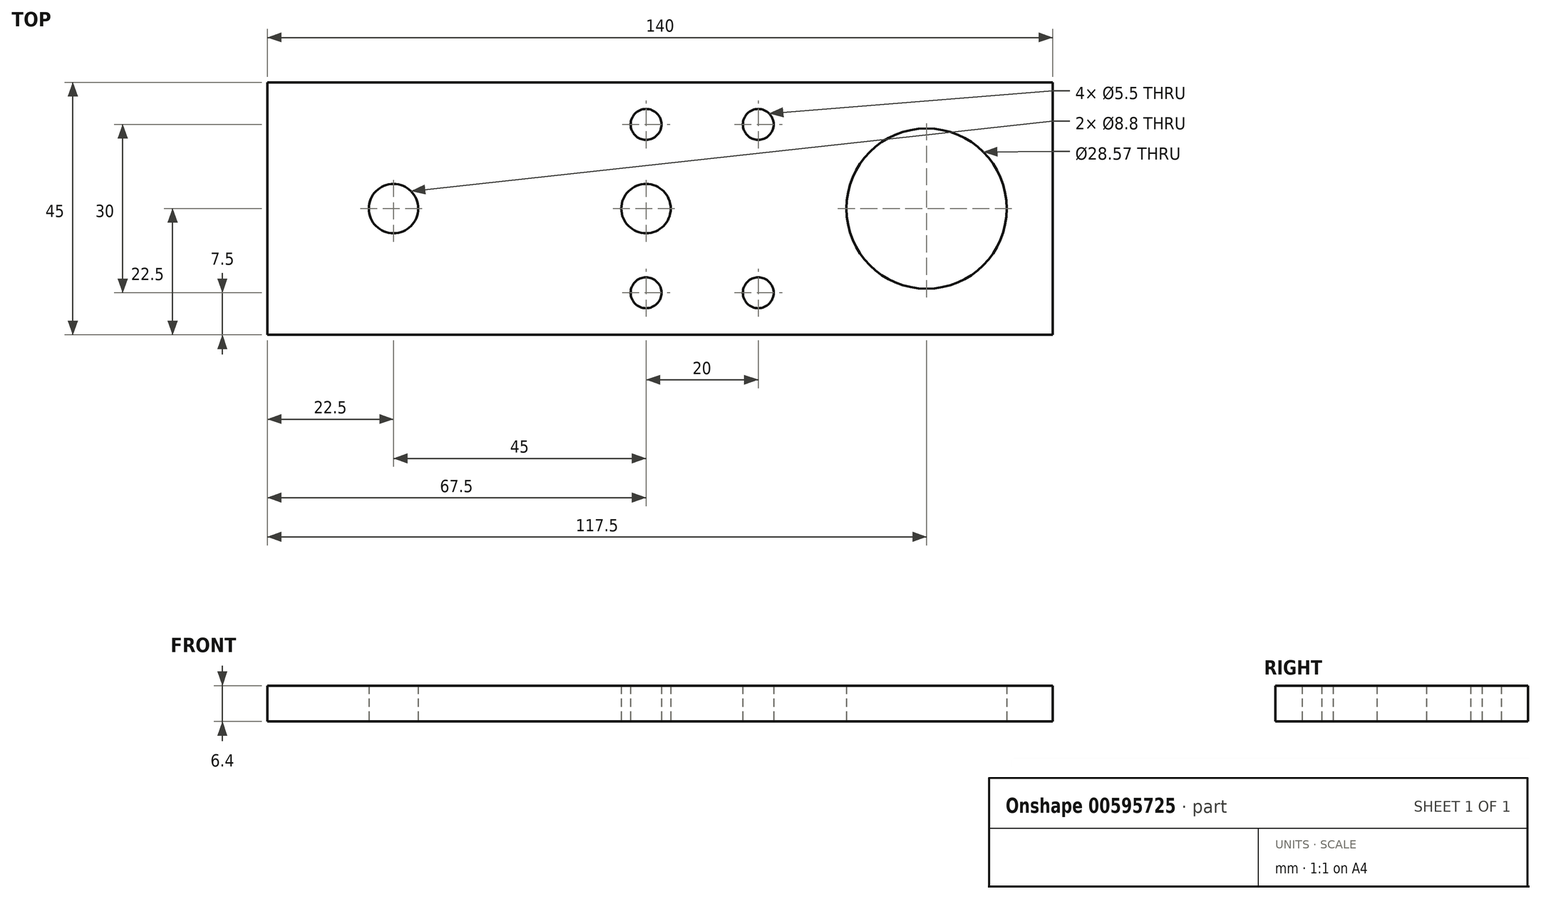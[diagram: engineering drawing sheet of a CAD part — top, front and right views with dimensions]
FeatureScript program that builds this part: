
annotation { "Feature Type Name" : "Feature", "Feature Type Description" : "" }
export const myFeature = defineFeature(function(context is Context, id is Id, definition is map)
    precondition{}
    {
        {
            var Q0;
            Q0=qCreatedBy(makeId("Top.planeOp"),FACE);
            var sketch = newSketch(context, id + "F0", { "sketchPlane" : qUnion([Q0])});
            skLineSegment(sketch, "E0.bottom", {"start": v(-70, 22.5) * mm, "end": v(70, 22.5) * mm});
            skLineSegment(sketch, "E0.top", {"start": v(-70, -22.5) * mm, "end": v(70, -22.5) * mm});
            skLineSegment(sketch, "E0.left", {"start": v(-70, 22.5) * mm, "end": v(-70, -22.5) * mm});
            skLineSegment(sketch, "E0.right", {"start": v(70, 22.5) * mm, "end": v(70, -22.5) * mm});
            skPoint(sketch, "E0.middle", {"position": v(0, 0) * mm});
            skCircle(sketch, "E1", {"center": v(47.5, 0) * mm, "radius": 14.29 * mm});
            skSolve(sketch);
        }
        {
            var Q0;
            Q0 = qSketchRegion(id + "F0", true);
            extrude(context, id + "F1", {"entities" : qUnion([Q0]), "depth" : 6.4 * mm, "offsetDistance" : 25 * mm});
        }
        {
            var Q0;
            Q0=makeQuery(id+"F1.opExtrude","CAP_FACE",FACE,{"disambiguationData":[OSD([sQuery(id+"F0.wireOp",EDGE,"E0.bottom"),sQuery(id+"F0.wireOp",EDGE,"E0.top"),sQuery(id+"F0.wireOp",EDGE,"E0.left"),sQuery(id+"F0.wireOp",EDGE,"E0.right"),sQuery(id+"F0.wireOp",EDGE,"E1")])],"isStart":true});
            var sketch = newSketch(context, id + "F2", { "sketchPlane" : qUnion([Q0])});
            skLineSegment(sketch, "E2.0", {"start": v(-70, -22.5) * mm, "end": v(-70, 22.5) * mm, "construction": true});
            skPoint(sketch, "E3", {"position": v(-2.5, 0) * mm});
            skPoint(sketch, "E4", {"position": v(-47.5, 0) * mm});
            skSolve(sketch);
        }
        {
            var Q0;
            Q0=sQuery(id+"F2.wireOp",VERTEX,"E4");
            var Q1;
            Q1=sQuery(id+"F2.wireOp",VERTEX,"E3");
            var Q2;
            Q2=makeQuery(id+"F1.opExtrude","SWEPT_BODY",BODY,{"disambiguationData":[OSD([sQuery(id+"F0.wireOp",EDGE,"E0.bottom"),sQuery(id+"F0.wireOp",EDGE,"E0.top"),sQuery(id+"F0.wireOp",EDGE,"E0.left"),sQuery(id+"F0.wireOp",EDGE,"E0.right"),sQuery(id+"F0.wireOp",EDGE,"E1")])]});
            hole(context, id + "F3", {"style" : HoleStyle.SIMPLE, "endStyle" : HoleEndStyle.THROUGH, "standardTappedOrClearance" : lookupTablePath({ "standard" : "ISO", "fit" : "Normal", "size" : "M8", "type" : "Clearance" }), "standardBlindInLast" : lookupTablePath({ "fit" : "Standard", "standard" : "ISO", "size" : "M8", "type" : "Clearance" }), "holeDiameter" : 8.8 * mm, "majorDiameter" : 5 * mm, "isTappedThrough" : true, "tappedDepth" : 12 * mm, "tapClearance" : 3, "locations" : qUnion([Q0, Q1]), "scope" : qUnion([Q2])});
        }
        {
            var Q0;
            Q0=qCreatedBy(makeId("Top.planeOp"),FACE);
            var sketch = newSketch(context, id + "F4", { "sketchPlane" : qUnion([Q0])});
            skCircle(sketch, "E5.0", {"center": v(-2.5, 0) * mm, "radius": 4.4 * mm, "construction": true});
            skLineSegment(sketch, "E6.bottom", {"start": v(-2.5, 15) * mm, "end": v(17.5, 15) * mm, "construction": true});
            skLineSegment(sketch, "E6.top", {"start": v(-2.5, -15) * mm, "end": v(17.5, -15) * mm, "construction": true});
            skLineSegment(sketch, "E6.left", {"start": v(-2.5, 15) * mm, "end": v(-2.5, -15) * mm, "construction": true});
            skLineSegment(sketch, "E6.right", {"start": v(17.5, 15) * mm, "end": v(17.5, -15) * mm, "construction": true});
            skPoint(sketch, "E6.middle", {"position": v(7.5, 0) * mm});
            skPoint(sketch, "E7", {"position": v(-2.5, 15) * mm});
            skPoint(sketch, "E8", {"position": v(17.5, 15) * mm});
            skPoint(sketch, "E9", {"position": v(17.5, -15) * mm});
            skPoint(sketch, "E10", {"position": v(-2.5, -15) * mm});
            skSolve(sketch);
        }
        {
            var Q0;
            Q0=sQuery(id+"F4.wireOp",VERTEX,"E7");
            var Q1;
            Q1=sQuery(id+"F4.wireOp",VERTEX,"E8");
            var Q2;
            Q2=sQuery(id+"F4.wireOp",VERTEX,"E9");
            var Q3;
            Q3=sQuery(id+"F4.wireOp",VERTEX,"E10");
            var Q4;
            Q4=makeQuery(id+"F1.opExtrude","SWEPT_BODY",BODY,{"disambiguationData":[OSD([sQuery(id+"F0.wireOp",EDGE,"E0.bottom"),sQuery(id+"F0.wireOp",EDGE,"E0.top"),sQuery(id+"F0.wireOp",EDGE,"E0.left"),sQuery(id+"F0.wireOp",EDGE,"E0.right"),sQuery(id+"F0.wireOp",EDGE,"E1")])]});
            hole(context, id + "F5", {"style" : HoleStyle.SIMPLE, "endStyle" : HoleEndStyle.BLIND, "oppositeDirection" : true, "standardTappedOrClearance" : lookupTablePath({ "standard" : "ISO", "fit" : "Normal", "size" : "M5", "type" : "Clearance" }), "standardBlindInLast" : lookupTablePath({ "fit" : "Standard", "standard" : "ISO", "size" : "M5", "type" : "Clearance" }), "holeDiameter" : 5.5 * mm, "majorDiameter" : 5 * mm, "holeDepth" : 13.5 * mm, "isTappedThrough" : true, "tappedDepth" : 12 * mm, "tapClearance" : 3, "locations" : qUnion([Q0, Q1, Q2, Q3]), "scope" : qUnion([Q4])});
        }
    });
